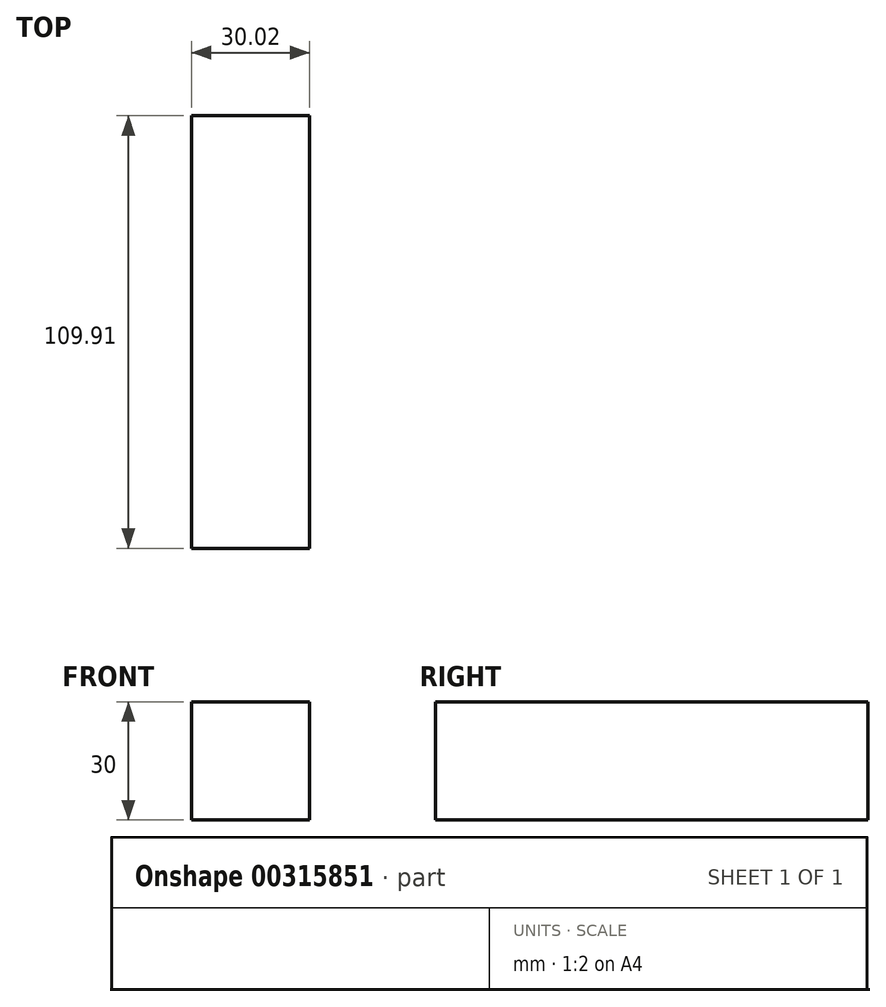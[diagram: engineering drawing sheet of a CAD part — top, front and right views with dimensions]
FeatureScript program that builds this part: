
annotation { "Feature Type Name" : "Feature", "Feature Type Description" : "" }
export const myFeature = defineFeature(function(context is Context, id is Id, definition is map)
    precondition{}
    {
        {
            var Q0;
            Q0=qCreatedBy(makeId("Top.planeOp"),FACE);
            var sketch = newSketch(context, id + "F0", { "sketchPlane" : qUnion([Q0])});
            skLineSegment(sketch, "E0.bottom", {"start": v(0, 7.93) * mm, "end": v(0, 7.93) * mm});
            skLineSegment(sketch, "E0.top", {"start": v(0, -7.93) * mm, "end": v(0, -7.93) * mm});
            skLineSegment(sketch, "E0.left", {"start": v(0, 7.93) * mm, "end": v(0, -7.93) * mm});
            skLineSegment(sketch, "E0.right", {"start": v(0, 7.93) * mm, "end": v(0, -7.93) * mm});
            skPoint(sketch, "E0.middle", {"position": v(0, 0) * mm});
            skLineSegment(sketch, "E1.bottom", {"start": v(-16.71, 65.44) * mm, "end": v(13.31, 65.44) * mm});
            skLineSegment(sketch, "E1.top", {"start": v(-16.71, -44.47) * mm, "end": v(13.31, -44.47) * mm});
            skLineSegment(sketch, "E1.left", {"start": v(-16.71, 65.44) * mm, "end": v(-16.71, -44.47) * mm});
            skLineSegment(sketch, "E1.right", {"start": v(13.31, 65.44) * mm, "end": v(13.31, -44.47) * mm});
            skPoint(sketch, "E1.middle", {"position": v(-1.7, 10.48) * mm});
            skSolve(sketch);
        }
        {
            var Q0;
            Q0 = qSketchRegion(id + "F0", true);
            extrude(context, id + "F1", {"entities" : qUnion([Q0]), "depth" : 30 * mm});
        }
    });
